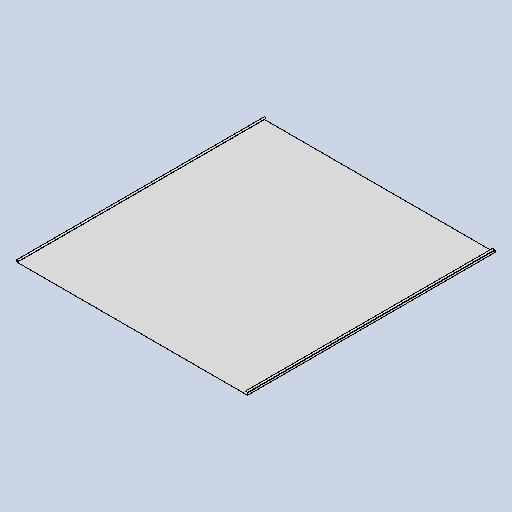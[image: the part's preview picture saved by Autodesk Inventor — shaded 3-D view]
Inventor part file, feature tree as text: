
AUTODESK INVENTOR PART (.ipt)
format: ipt  version: 2025 (Build 290162010, 162A)  size: 201,728 bytes
history: native  units: mm
features: sheet_metal_op x7, sketch x4, other x4, extrude x1, chamfer x1, projected_geometry x1
ambient origin geometry x8: Origin, YZ Plane, XZ Plane, XY Plane, X Axis, Y Axis, Z Axis, Center Point
bodies: Body1 (feature_tree)
feature tree (18):
  sheet_metal_op  "Face1"
  sheet_metal_op  "Flange1"
  sheet_metal_op  "Flange2"
  extrude  "Extrusion3"  Depth=915.0mm
  chamfer  "Corner Round1"
  sketch  "Sketch6"  dims[d12=23.212879mm d52=915.0mm]
  other  "Plate2"
  sketch  "Sketch10"  dims[d53=980.0mm]
  other  "Plate3"
  sheet_metal_op  "Bend2"
  sheet_metal_op  "Corner2"
  sketch  "Sketch11"  dims[d54=0.5mm]
  other  "Plate4"
  sheet_metal_op  "Bend3"
  sheet_metal_op  "Corner3"
  sketch  "Sketch12"  dims[d74=0.5mm d75=0.25mm d76=1.0mm d77=0.5mm d78=10.0mm d79=90.0deg d80=0.5mm d81=2.0mm d82=0.5mm d83=0.5mm d84=0.5mm d85=0.25mm d86=1.0mm d87=0.5mm d88=10.0mm d89=90.0deg d90=0.5mm d91=2.0mm d92=0.5mm d93=0.5mm d94=0.0mm d95=0.0mm d96=100.0mm d97=40.0mm d98=100.0mm d99=40.0mm d100=4.0mm]
  projected_geometry  "Projected Loop5"
  other  "Definition1"
